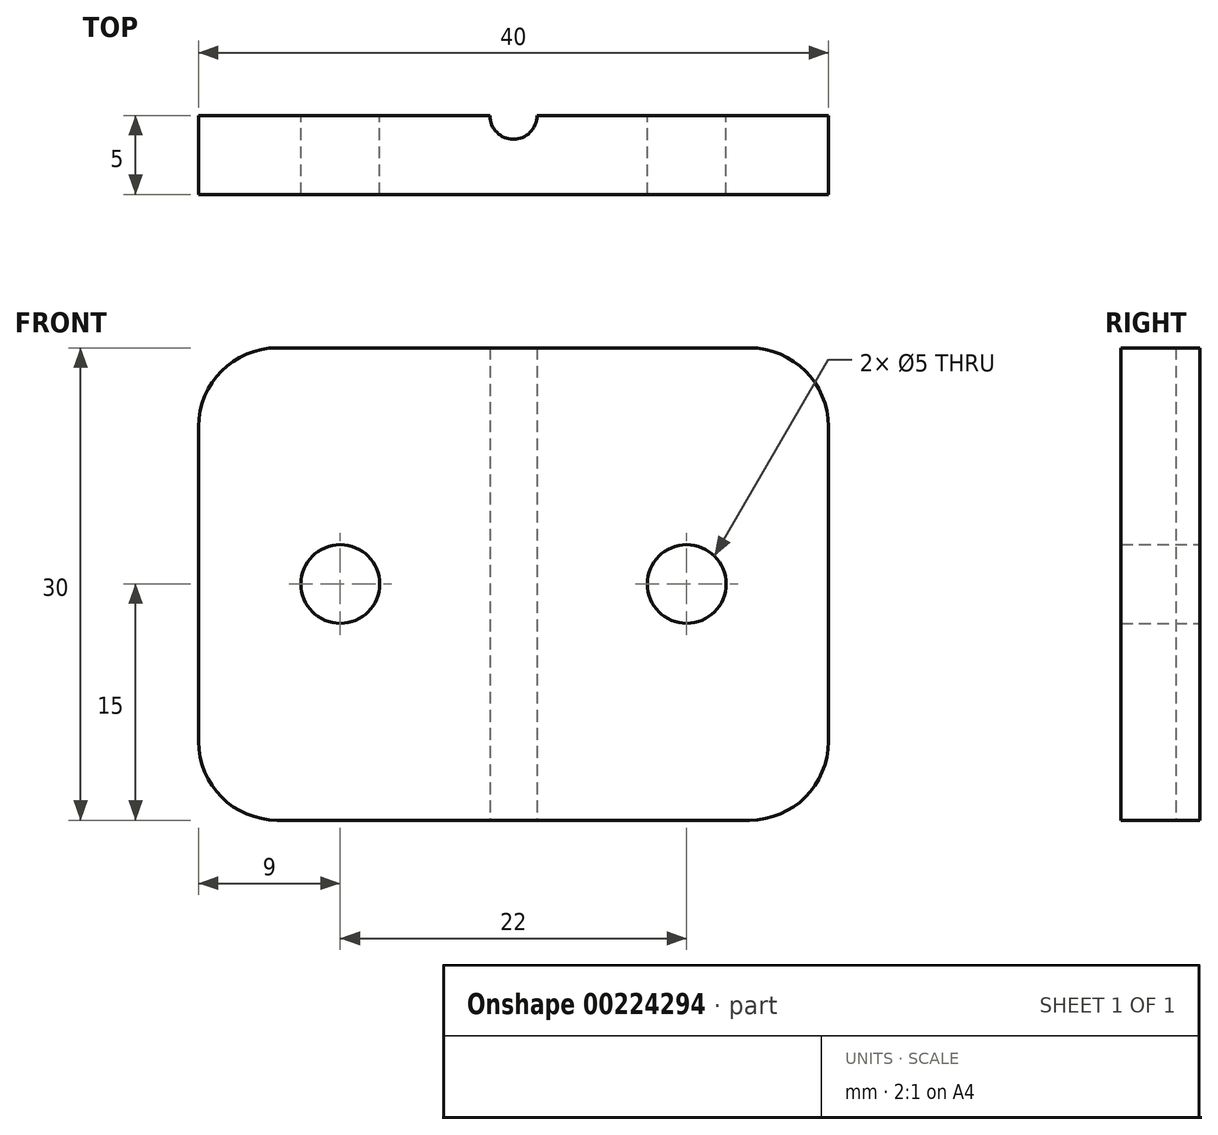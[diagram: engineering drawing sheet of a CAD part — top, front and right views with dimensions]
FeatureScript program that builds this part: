
annotation { "Feature Type Name" : "Feature", "Feature Type Description" : "" }
export const myFeature = defineFeature(function(context is Context, id is Id, definition is map)
    precondition{}
    {
        {
            var Q0;
            Q0=qCreatedBy(makeId("Front.planeOp"),FACE);
            var sketch = newSketch(context, id + "F0", { "sketchPlane" : qUnion([Q0])});
            skLineSegment(sketch, "E0.bottom", {"start": v(-20, 15) * mm, "end": v(20, 15) * mm});
            skLineSegment(sketch, "E0.top", {"start": v(-20, -15) * mm, "end": v(20, -15) * mm});
            skLineSegment(sketch, "E0.left", {"start": v(-20, 15) * mm, "end": v(-20, -15) * mm});
            skLineSegment(sketch, "E0.right", {"start": v(20, 15) * mm, "end": v(20, -15) * mm});
            skPoint(sketch, "E0.middle", {"position": v(0, 0) * mm});
            skCircle(sketch, "E1", {"center": v(-11, 0) * mm, "radius": 2.5 * mm});
            skCircle(sketch, "E2", {"center": v(11, 0) * mm, "radius": 2.5 * mm});
            skSolve(sketch);
        }
        {
            var Q0;
            Q0=makeQuery(id+"F0.imprint","IMPRINT",FACE,{"disambiguationData":[TD([[makeQuery(id+"F0.imprint","IMPRINT",EDGE,{"derivedFrom":sQuery(id+"F0.wireOp",EDGE,"E0.bottom")}),-1.0]])]});
            extrude(context, id + "F1", {"entities" : qUnion([Q0]), "depth" : 5 * mm});
        }
        {
            var Q0;
            Q0=makeQuery(id+"F1.opExtrude","SWEPT_FACE",FACE,{"disambiguationData":[OSD([sQuery(id+"F0.wireOp",EDGE,"E0.top")])]});
            var sketch = newSketch(context, id + "F2", { "sketchPlane" : qUnion([Q0])});
            skCircle(sketch, "E3", {"center": v(0, 0) * mm, "radius": 1.5 * mm});
            skSolve(sketch);
        }
        {
            var Q0;
            {var subQ0=sQuery(id+"F2.wireOp",EDGE,"E3");var subQ1=makeQuery(id+"F1.opExtrude","CAP_EDGE",EDGE,{"disambiguationData":[OSD([sQuery(id+"F0.wireOp",EDGE,"E0.top")])],"isStart":true});var subQ2=makeQuery(id+"F2.imprint","INTERSECT",VERTEX,{"disambiguationData":[OD(0.0)],"derivedFrom":[subQ1,subQ0]});Q0=makeQuery(id+"F2.imprint","IMPRINT",FACE,{"disambiguationData":[TD([[makeQuery(id+"F2.imprint","IMPRINT",EDGE,{"disambiguationData":[TD([[subQ2,1.0]])],"derivedFrom":subQ0}),1.0]])]});}
            extrude(context, id + "F3", {"entities" : qUnion([Q0]), "operationType" : NewBodyOperationType.REMOVE, "oppositeDirection" : true, "depth" : 31 * mm});
        }
        {
            var Q0;
            Q0=makeQuery(id+"F1.opExtrude","SWEPT_EDGE",EDGE,{"disambiguationData":[OSD([sQuery(id+"F0.wireOp",EDGE,"E0.top"),sQuery(id+"F0.wireOp",EDGE,"E0.right")])]});
            var Q1;
            Q1=makeQuery(id+"F1.opExtrude","SWEPT_EDGE",EDGE,{"disambiguationData":[OSD([sQuery(id+"F0.wireOp",EDGE,"E0.top"),sQuery(id+"F0.wireOp",EDGE,"E0.left")])]});
            var Q2;
            Q2=makeQuery(id+"F1.opExtrude","SWEPT_EDGE",EDGE,{"disambiguationData":[OSD([sQuery(id+"F0.wireOp",EDGE,"E0.bottom"),sQuery(id+"F0.wireOp",EDGE,"E0.right")])]});
            var Q3;
            Q3=makeQuery(id+"F1.opExtrude","SWEPT_EDGE",EDGE,{"disambiguationData":[OSD([sQuery(id+"F0.wireOp",EDGE,"E0.bottom"),sQuery(id+"F0.wireOp",EDGE,"E0.left")])]});
            fillet(context, id + "F4", {"entities" : qUnion([Q0, Q1, Q2, Q3]), "radius" : 5 * mm, "tangentPropagation" : true, "allowEdgeOverflow" : false});
        }
    });
